# Revit family: LR1730
name_source: partatom
category: Mechanical Equipment
revit_build: Autodesk Revit MEP 2016 (Build: 20150220_1215(x64)
units: mm (PartAtom-declared; Revit-internal decimal feet)

## family parameters
Cut with Voids When Loaded = No
Host = Face
OmniClass Number = 23.45.05.14.17
OmniClass Title = Showers
Part Type = Normal
Room Calculation Point = No
Round Connector Dimension = Use Diameter
Shared = Yes

## types (1)
- LR1730
    Amperage = 0
    CW Connection = Yes
    Default Elevation = 0 "
    Description = Ligature Resistant Cabinet Shower
    HW Connection = Yes
    Manufacturer = Acorn Engineering Co
    Material = Stainless Steel
    Model = LR1730
    OVERALL DEPTH = 30
    OVERALL SIZE HEIGHT = 88
    OVERALL SIZE WIDTH = 30
    Revised Date = 12/04/19
    Tempered Water Connection = No
    URL = http://www.murdockmfg.com
    Vent Connection = No
    Voltage = 0
    Waste Connection = Yes

## geometry (parser evidence)
native form markers: Sweep x6
no freeform markers — native parametric forms only
